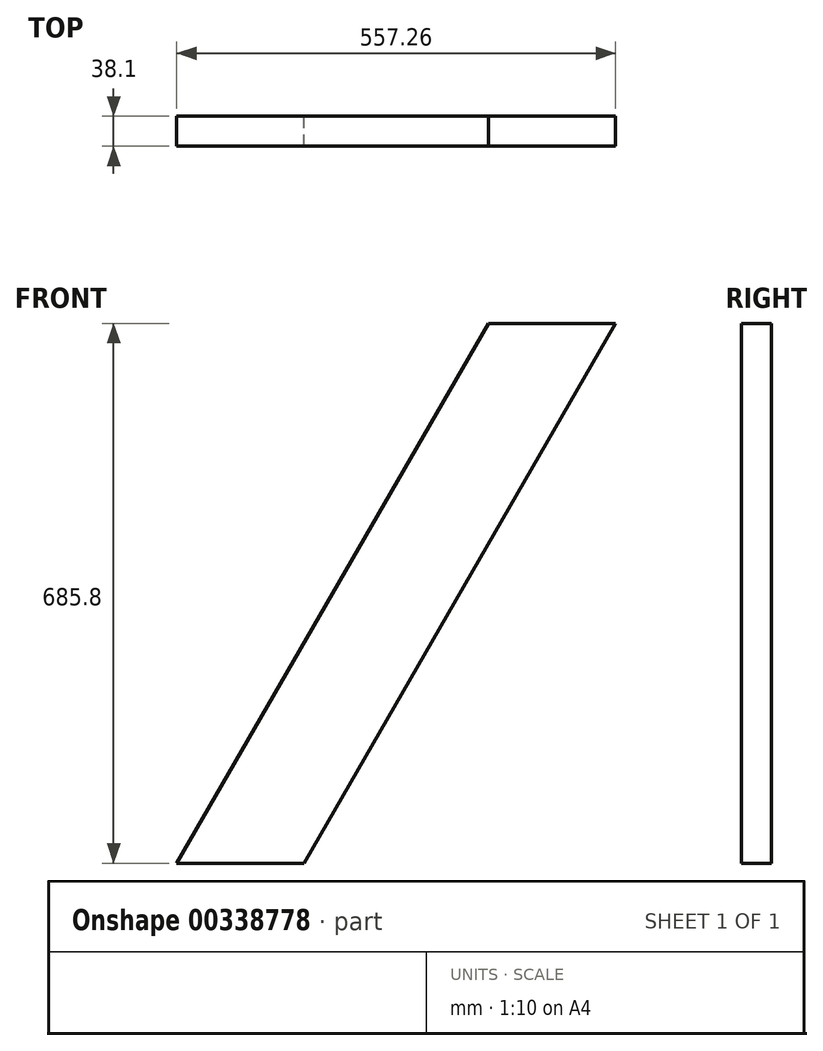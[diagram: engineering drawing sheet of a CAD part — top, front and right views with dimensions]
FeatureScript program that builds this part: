
annotation { "Feature Type Name" : "Feature", "Feature Type Description" : "" }
export const myFeature = defineFeature(function(context is Context, id is Id, definition is map)
    precondition{}
    {
        {
            var Q0;
            Q0=qCreatedBy(makeId("Front.planeOp"),FACE);
            var sketch = newSketch(context, id + "F0", { "sketchPlane" : qUnion([Q0])});
            skLineSegment(sketch, "E0", {"start": v(0, 0) * mm, "end": v(395.95, 685.8) * mm});
            skLineSegment(sketch, "E1", {"start": v(395.95, 685.8) * mm, "end": v(557.26, 685.8) * mm});
            skLineSegment(sketch, "E2", {"start": v(557.26, 685.8) * mm, "end": v(161.31, 0) * mm});
            skLineSegment(sketch, "E3", {"start": v(161.31, 0) * mm, "end": v(0, 0) * mm});
            skSolve(sketch);
        }
        {
            var Q0;
            Q0=makeQuery(id+"F0.imprint","IMPRINT",FACE,{"disambiguationData":[TD([[makeQuery(id+"F0.imprint","IMPRINT",EDGE,{"derivedFrom":sQuery(id+"F0.wireOp",EDGE,"E0")}),-1.0]])]});
            extrude(context, id + "F1", {"entities" : qUnion([Q0]), "depth" : 38.1 * mm});
        }
    });
